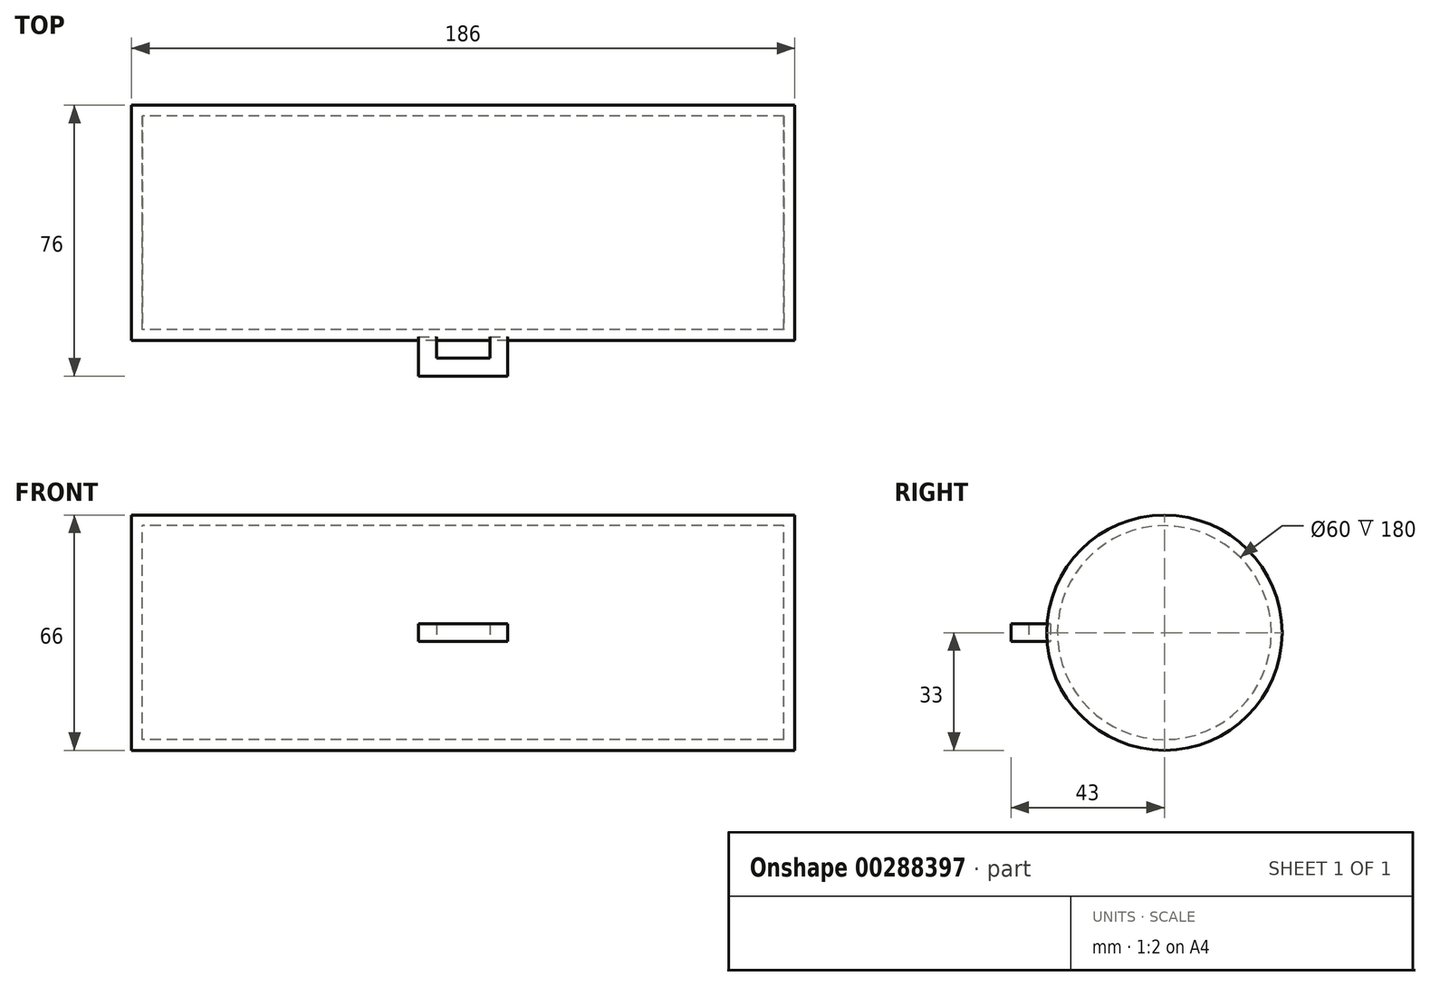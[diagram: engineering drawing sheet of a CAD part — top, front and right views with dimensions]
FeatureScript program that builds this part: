
annotation { "Feature Type Name" : "Feature", "Feature Type Description" : "" }
export const myFeature = defineFeature(function(context is Context, id is Id, definition is map)
    precondition{}
    {
        {
            var Q0;
            Q0=qCreatedBy(makeId("Right.planeOp"),FACE);
            var sketch = newSketch(context, id + "F0", { "sketchPlane" : qUnion([Q0])});
            skCircle(sketch, "E0", {"center": v(0, 0) * mm, "radius": 33 * mm});
            skSolve(sketch);
        }
        {
            var Q0;
            Q0 = qSketchRegion(id + "F0", true);
            extrude(context, id + "F1", {"entities" : qUnion([Q0]), "depth" : 186 * mm});
        }
        {
            var Q0;
            Q0=makeQuery(id+"F1.opExtrude","SWEPT_FACE",FACE,{"disambiguationData":[OSD([sQuery(id+"F0.wireOp",EDGE,"E0")])]});
            var Q1;
            Q1=makeQuery(id+"F1.opExtrude","SWEPT_BODY",BODY,{"disambiguationData":[OSD([sQuery(id+"F0.wireOp",EDGE,"E0")])]});
            shell(context, id + "F2", {"isHollow" : true, "entities" : qUnion([Q0]), "parts" : qUnion([Q1]), "thickness" : 3 * mm});
        }
        {
            var Q0;
            Q0=qCreatedBy(makeId("Top.planeOp"),FACE);
            var sketch = newSketch(context, id + "F3", { "sketchPlane" : qUnion([Q0])});
            skLineSegment(sketch, "E1.top", {"start": v(80.5, -43) * mm, "end": v(105.5, -43) * mm});
            skLineSegment(sketch, "E1.left", {"start": v(80.5, -32) * mm, "end": v(80.5, -43) * mm});
            skLineSegment(sketch, "E1.right", {"start": v(105.5, -32) * mm, "end": v(105.5, -43) * mm});
            skLineSegment(sketch, "E2", {"start": v(80.5, -32) * mm, "end": v(85.5, -32) * mm});
            skLineSegment(sketch, "E3", {"start": v(85.5, -32) * mm, "end": v(85.5, -38) * mm});
            skLineSegment(sketch, "E4", {"start": v(85.5, -38) * mm, "end": v(100.5, -38) * mm});
            skLineSegment(sketch, "E5", {"start": v(100.5, -38) * mm, "end": v(100.5, -32) * mm});
            skLineSegment(sketch, "E6", {"start": v(100.5, -32) * mm, "end": v(105.5, -32) * mm});
            skSolve(sketch);
        }
        {
            var Q0;
            Q0=makeQuery(id+"F3.imprint","IMPRINT",FACE,{"disambiguationData":[TD([[makeQuery(id+"F3.imprint","IMPRINT",EDGE,{"derivedFrom":sQuery(id+"F3.wireOp",EDGE,"E1.top")}),1.0]])]});
            extrude(context, id + "F4", {"entities" : qUnion([Q0]), "depth" : 5 * mm});
        }
        {
            var Q0;
            Q0=makeQuery(id+"F4.opExtrude","SWEPT_BODY",BODY,{"disambiguationData":[OSD([sQuery(id+"F3.wireOp",EDGE,"E1.top"),sQuery(id+"F3.wireOp",EDGE,"E1.left"),sQuery(id+"F3.wireOp",EDGE,"E1.right"),sQuery(id+"F3.wireOp",EDGE,"E2"),sQuery(id+"F3.wireOp",EDGE,"E3"),sQuery(id+"F3.wireOp",EDGE,"E4"),sQuery(id+"F3.wireOp",EDGE,"E5"),sQuery(id+"F3.wireOp",EDGE,"E6")])]});
            transform(context, id + "F5", {"entities" : qUnion([Q0]), "transformType" : TransformType.TRANSLATION_3D, "dx" : 0 * mm, "dy" : 0 * mm, "dz" : -2.5 * mm, "makeCopy" : false});
        }
    });
